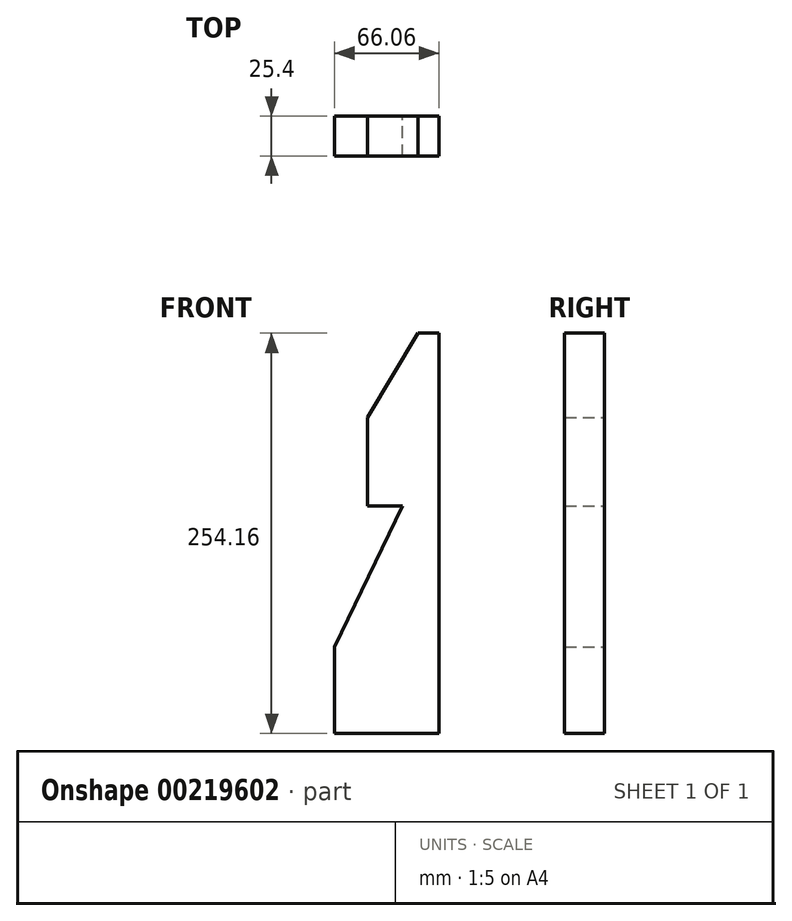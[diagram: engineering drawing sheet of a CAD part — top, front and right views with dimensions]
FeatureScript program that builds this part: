
annotation { "Feature Type Name" : "Feature", "Feature Type Description" : "" }
export const myFeature = defineFeature(function(context is Context, id is Id, definition is map)
    precondition{}
    {
        {
            var Q0;
            Q0=qCreatedBy(makeId("Front.planeOp"),FACE);
            var sketch = newSketch(context, id + "F0", { "sketchPlane" : qUnion([Q0])});
            skLineSegment(sketch, "E0", {"start": v(33.03, -127.08) * mm, "end": v(33.03, 127.08) * mm});
            skLineSegment(sketch, "E1", {"start": v(33.03, 127.08) * mm, "end": v(19.98, 127.08) * mm});
            skLineSegment(sketch, "E2", {"start": v(19.98, 127.08) * mm, "end": v(-12.2, 73.48) * mm});
            skLineSegment(sketch, "E3", {"start": v(-12.2, 73.48) * mm, "end": v(-12.2, 17.36) * mm});
            skLineSegment(sketch, "E4", {"start": v(-12.2, 17.36) * mm, "end": v(9.88, 17.36) * mm});
            skLineSegment(sketch, "E5", {"start": v(9.88, 17.36) * mm, "end": v(-33.03, -72.18) * mm});
            skLineSegment(sketch, "E6", {"start": v(-33.03, -72.18) * mm, "end": v(-33.03, -127.08) * mm});
            skLineSegment(sketch, "E7", {"start": v(-33.03, -127.08) * mm, "end": v(33.03, -127.08) * mm});
            skSolve(sketch);
        }
        {
            var Q0;
            Q0=makeQuery(id+"F0.imprint","IMPRINT",FACE,{"disambiguationData":[TD([[makeQuery(id+"F0.imprint","IMPRINT",EDGE,{"derivedFrom":sQuery(id+"F0.wireOp",EDGE,"E0")}),1.0]])]});
            extrude(context, id + "F1", {"entities" : qUnion([Q0]), "depth" : 25.4 * mm});
        }
    });
